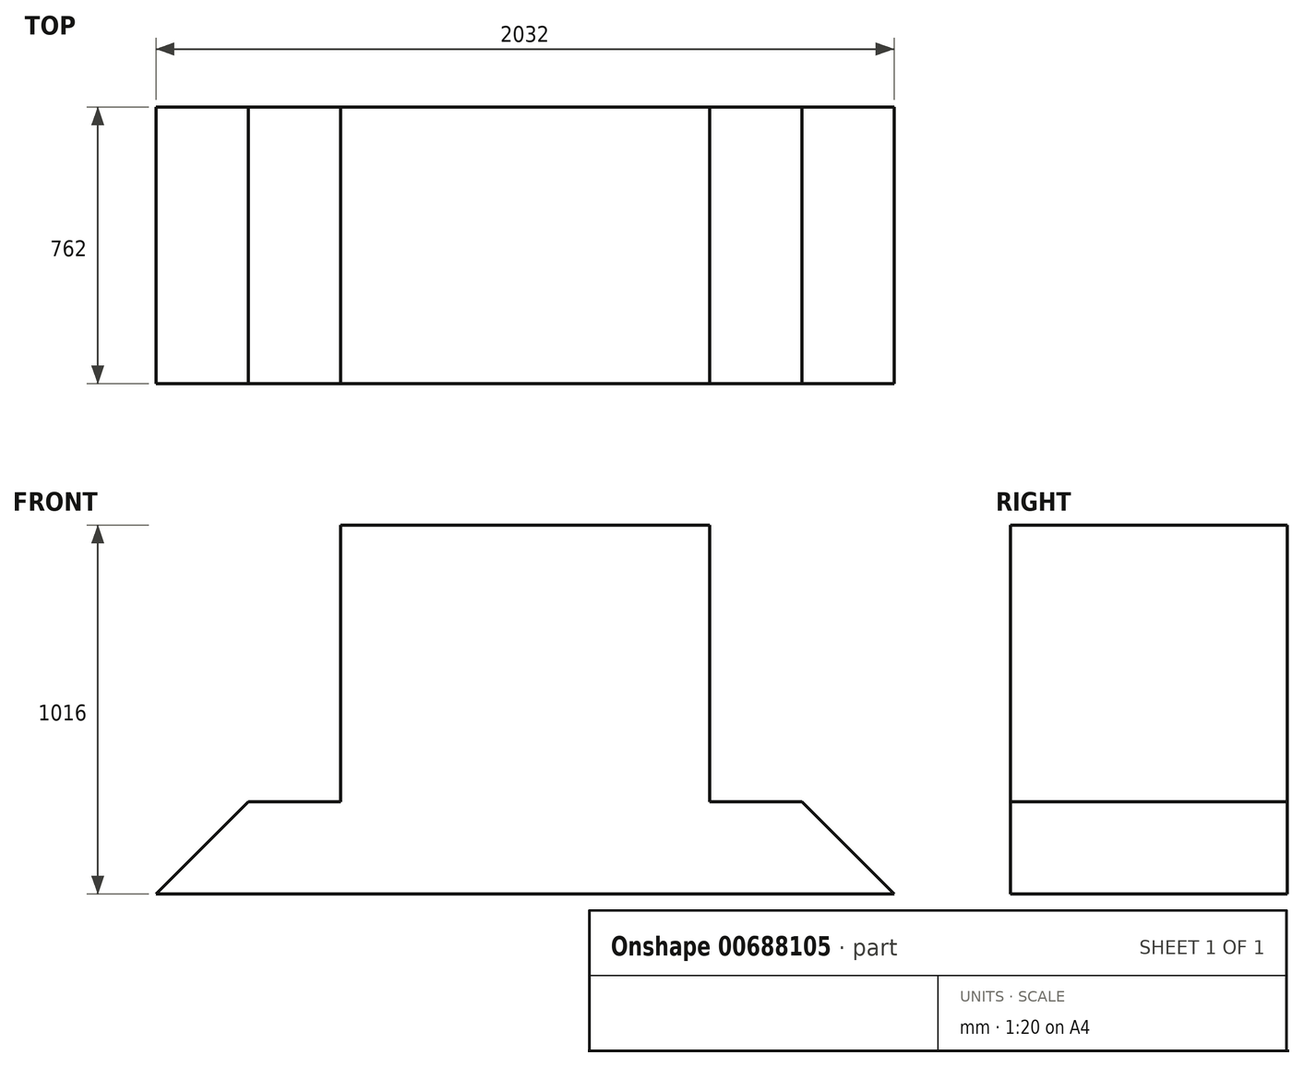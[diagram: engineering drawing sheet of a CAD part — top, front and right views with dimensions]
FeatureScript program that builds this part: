
annotation { "Feature Type Name" : "Feature", "Feature Type Description" : "" }
export const myFeature = defineFeature(function(context is Context, id is Id, definition is map)
    precondition{}
    {
        {
            var Q0;
            Q0=qCreatedBy(makeId("Front.planeOp"),FACE);
            var sketch = newSketch(context, id + "F0", { "sketchPlane" : qUnion([Q0])});
            skLineSegment(sketch, "E0", {"start": v(0, 0) * mm, "end": v(2032, 0) * mm});
            skLineSegment(sketch, "E1", {"start": v(2032, 0) * mm, "end": v(1778, 254) * mm});
            skLineSegment(sketch, "E2", {"start": v(0, 0) * mm, "end": v(254, 254) * mm});
            skLineSegment(sketch, "E3", {"start": v(254, 254) * mm, "end": v(508, 254) * mm});
            skLineSegment(sketch, "E4", {"start": v(1778, 254) * mm, "end": v(1524, 254) * mm});
            skLineSegment(sketch, "E5", {"start": v(508, 254) * mm, "end": v(508, 1016) * mm});
            skLineSegment(sketch, "E6", {"start": v(1524, 254) * mm, "end": v(1524, 1016) * mm});
            skLineSegment(sketch, "E7", {"start": v(508, 1016) * mm, "end": v(1524, 1016) * mm});
            skSolve(sketch);
        }
        {
            var Q0;
            Q0 = qSketchRegion(id + "F0", true);
            extrude(context, id + "F1", {"entities" : qUnion([Q0]), "depth" : 762 * mm, "offsetDistance" : 25.4 * mm});
        }
    });
